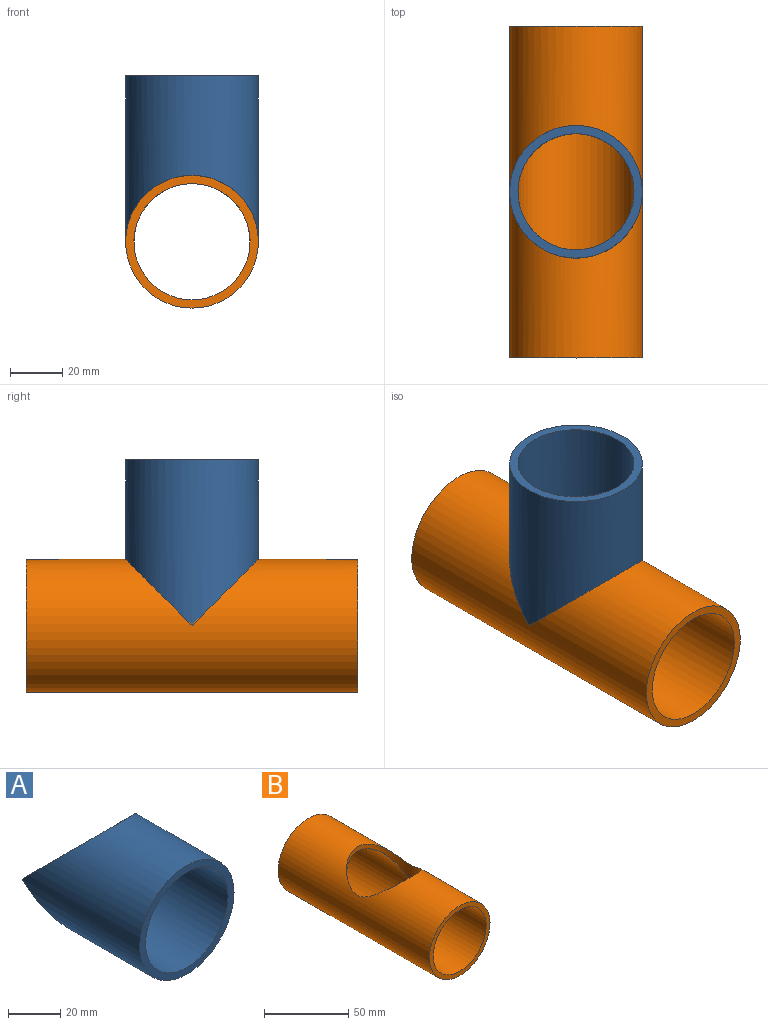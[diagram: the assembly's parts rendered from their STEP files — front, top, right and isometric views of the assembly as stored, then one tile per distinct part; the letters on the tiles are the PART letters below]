
ASSEMBLY  parts=2 mates=1
PART A: 4 faces, bbox 50.8x63.5x51 mm
  f0: cylinder r=22.23mm len=51.21mm, axis (0,1,0), area 6154.5mm2, adj f2,f3
  f1: cylinder r=25.4mm len=63.5mm, axis (0,1,0), area 7553.5mm2, adj f2,f3
  f2: plane 50.8x50.8mm, normal (0,-1,0), area 475mm2, adj f0,f1
  f3: cylinder r=25.4mm len=50.97mm, axis (0,0,1), area 800.9mm2, adj f0,f1
PART B: 5 faces, bbox 50.8x127x50.8 mm
  f0: cylinder r=22.23mm len=127mm, axis (0,1,0), area 15759mm2, adj f2,f3,f4
  f1: cylinder r=25.4mm len=127mm, axis (0,1,0), area 18490.7mm2, adj f2,f3,f4
  f2: plane 50.8x50.8mm, normal (0,-1,0), area 475mm2, adj f0,f1
  f3: plane 50.8x50.8mm, normal (0,1,0), area 475mm2, adj f0,f1
  f4: cylinder r=22.23mm len=44.45mm, axis (0,0,1), area 736.7mm2, adj f0,f1
PLACE A rot(axis=(-1,0,0),90deg) t=(71.59,-63.5,0)mm
PLACE B t=(71.59,0,0)mm
MATE fastened A.f3 <-> B.f1  axis (0,1,0) through (71.59,-63.5,0)mm
